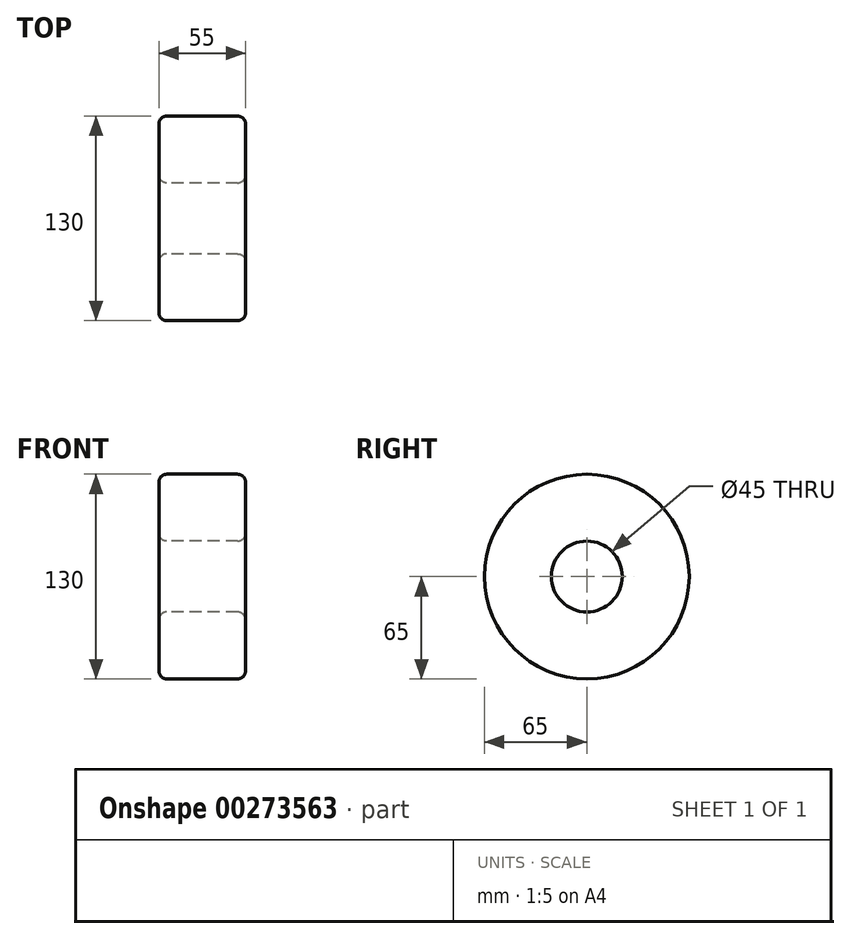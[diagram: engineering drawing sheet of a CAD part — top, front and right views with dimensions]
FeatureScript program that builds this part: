
annotation { "Feature Type Name" : "Feature", "Feature Type Description" : "" }
export const myFeature = defineFeature(function(context is Context, id is Id, definition is map)
    precondition{}
    {
        {
            var Q0;
            Q0=qCreatedBy(makeId("Right.planeOp"),FACE);
            var sketch = newSketch(context, id + "F0", { "sketchPlane" : qUnion([Q0])});
            skCircle(sketch, "E0", {"center": v(0, 0) * mm, "radius": 65 * mm});
            skCircle(sketch, "E1", {"center": v(0, 0) * mm, "radius": 22.5 * mm});
            skSolve(sketch);
        }
        {
            var Q0;
            Q0 = qSketchRegion(id + "F0", true);
            extrude(context, id + "F1", {"entities" : qUnion([Q0]), "depth" : 55 * mm});
        }
        {
            var Q0;
            Q0=makeQuery(id+"F1.opExtrude","SWEPT_FACE",FACE,{"disambiguationData":[OSD([sQuery(id+"F0.wireOp",EDGE,"E0")])]});
            var Q1;
            Q1=makeQuery(id+"F1.opExtrude","SWEPT_FACE",FACE,{"disambiguationData":[OSD([sQuery(id+"F0.wireOp",EDGE,"E1")])]});
            fillet(context, id + "F2", {"entities" : qUnion([Q0, Q1]), "radius" : 5 * mm, "tangentPropagation" : true, "allowEdgeOverflow" : false});
        }
    });
